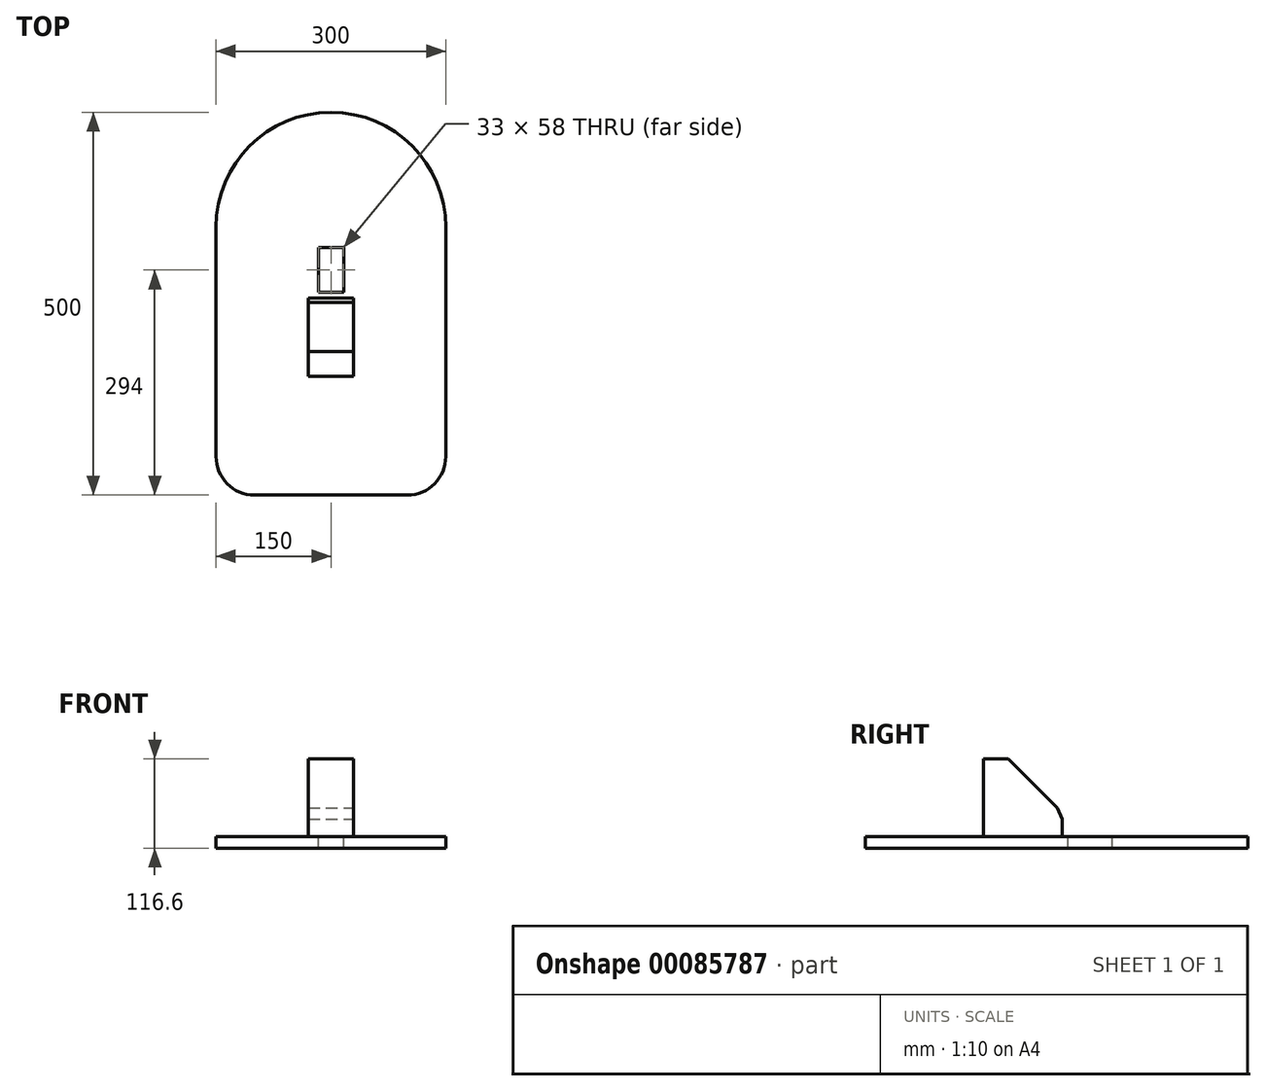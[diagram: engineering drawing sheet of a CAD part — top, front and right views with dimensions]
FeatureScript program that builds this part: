
annotation { "Feature Type Name" : "Feature", "Feature Type Description" : "" }
export const myFeature = defineFeature(function(context is Context, id is Id, definition is map)
    precondition{}
    {
        {
            var Q0;
            Q0=qCreatedBy(makeId("Top.planeOp"),FACE);
            var sketch = newSketch(context, id + "F0", { "sketchPlane" : qUnion([Q0])});
            skLineSegment(sketch, "E0.rect.bottom", {"start": v(100, -250) * mm, "end": v(-100, -250) * mm});
            skLineSegment(sketch, "E0.rect.left", {"start": v(150, -200) * mm, "end": v(150, 100) * mm});
            skLineSegment(sketch, "E0.rect.right", {"start": v(-150, -250) * mm, "end": v(-150, 100) * mm});
            skPoint(sketch, "E0.rect.middle", {"position": v(0, 0) * mm});
            skPoint(sketch, "E1.orphan", {"position": v(-150, 250) * mm});
            skPoint(sketch, "E2.orphan", {"position": v(150, 250) * mm});
            skArc(sketch, "E3", {"start": v(150, 100) * mm, "mid": v(0, 250) * mm, "end": v(-150, 100) * mm});
            skPoint(sketch, "E4.start.orphan", {"position": v(0, 250) * mm});
            skPoint(sketch, "E5.start.orphan", {"position": v(-100, 250) * mm});
            skPoint(sketch, "E6.end.orphan", {"position": v(100, 250) * mm});
            skArc(sketch, "E7", {"start": v(-150, -200) * mm, "mid": v(-135.36, -235.36) * mm, "end": v(-100, -250) * mm});
            skArc(sketch, "E8", {"start": v(100, -250) * mm, "mid": v(135.36, -235.36) * mm, "end": v(150, -200) * mm});
            skPoint(sketch, "E9.orphan", {"position": v(150, -250) * mm});
            skSolve(sketch);
        }
        {
            var Q0;
            Q0=qSketchRegion(id+"F0",true);
            extrude(context, id + "F1", {"entities" : qUnion([Q0]), "depth" : 15 * mm});
        }
        {
            var Q0;
            Q0=makeQuery(id+"F1.opExtrude","CAP_FACE",FACE,{"disambiguationData":[OSD([sQuery(id+"F0.wireOp",EDGE,"E0.rect.bottom"),sQuery(id+"F0.wireOp",EDGE,"E0.rect.left"),sQuery(id+"F0.wireOp",EDGE,"E0.rect.right"),sQuery(id+"F0.wireOp",EDGE,"E3"),sQuery(id+"F0.wireOp",EDGE,"E7"),sQuery(id+"F0.wireOp",EDGE,"E8")])],"isStart":false});
            var sketch = newSketch(context, id + "F2", { "sketchPlane" : qUnion([Q0])});
            skLineSegment(sketch, "E10.bottom", {"start": v(-16.5, 73) * mm, "end": v(16.5, 73) * mm});
            skLineSegment(sketch, "E10.top", {"start": v(-16.5, 15) * mm, "end": v(16.5, 15) * mm});
            skLineSegment(sketch, "E10.left", {"start": v(-16.5, 73) * mm, "end": v(-16.5, 15) * mm});
            skLineSegment(sketch, "E10.right", {"start": v(16.5, 73) * mm, "end": v(16.5, 15) * mm});
            skLineSegment(sketch, "E11", {"start": v(150, 100) * mm, "end": v(-52.78, 100) * mm});
            skSolve(sketch);
        }
        {
            var Q0;
            Q0=qSketchRegion(id+"F2",true);
            extrude(context, id + "F3", {"entities" : qUnion([Q0]), "operationType" : NewBodyOperationType.REMOVE, "endBound" : BoundingType.THROUGH_ALL, "oppositeDirection" : true, "depth" : 25 * mm});
        }
        {
            var Q0;
            Q0=makeQuery(id+"F1.opExtrude","CAP_FACE",FACE,{"disambiguationData":[OSD([sQuery(id+"F0.wireOp",EDGE,"E0.rect.bottom"),sQuery(id+"F0.wireOp",EDGE,"E0.rect.left"),sQuery(id+"F0.wireOp",EDGE,"E0.rect.right"),sQuery(id+"F0.wireOp",EDGE,"E3"),sQuery(id+"F0.wireOp",EDGE,"E7"),sQuery(id+"F0.wireOp",EDGE,"E8")])],"isStart":false});
            var sketch = newSketch(context, id + "F4", { "sketchPlane" : qUnion([Q0])});
            skLineSegment(sketch, "E12.bottom", {"start": v(-29.4, -95.17) * mm, "end": v(29.4, -95.17) * mm});
            skLineSegment(sketch, "E12.top", {"start": v(-29.4, 7.1) * mm, "end": v(29.4, 7.1) * mm});
            skLineSegment(sketch, "E12.left", {"start": v(-29.4, -95.17) * mm, "end": v(-29.4, 7.1) * mm});
            skLineSegment(sketch, "E12.right", {"start": v(29.4, -95.17) * mm, "end": v(29.4, 7.1) * mm});
            skPoint(sketch, "E12.middle", {"position": v(0, -44.03) * mm});
            skSolve(sketch);
        }
        {
            var Q0;
            Q0 = qSketchRegion(id + "F4", true);
            extrude(context, id + "F5", {"entities" : qUnion([Q0]), "operationType" : NewBodyOperationType.ADD, "depth" : 101.6 * mm});
        }
        {
            var Q0;
            Q0=makeQuery(id+"F5.opExtrude","CAP_EDGE",EDGE,{"disambiguationData":[OSD([sQuery(id+"F4.wireOp",EDGE,"E12.top")])],"isStart":false});
            chamfer(context, id + "F6", {"entities" : qUnion([Q0]), "width" : 70 * mm, "tangentPropagation" : true});
        }
        {
            var Q0;
            {var subQ0=sQuery(id+"F4.wireOp",EDGE,"E12.top");Q0=makeQuery(id+"F6.opChamfer","BLEND_EDGE",EDGE,{"blendedFrom":[makeQuery(id+"F5.opExtrude","CAP_EDGE",EDGE,{"disambiguationData":[OSD([subQ0])],"isStart":false}),makeQuery(id+"F5.opExtrude","SWEPT_FACE",FACE,{"disambiguationData":[OSD([subQ0])]})],"blendedInto":[makeQuery(id+"F5.opExtrude","SWEPT_FACE",FACE,{"disambiguationData":[OSD([subQ0])]})]});}
            chamfer(context, id + "F7", {"entities" : qUnion([Q0]), "width" : 20 * mm, "tangentPropagation" : true});
        }
    });
